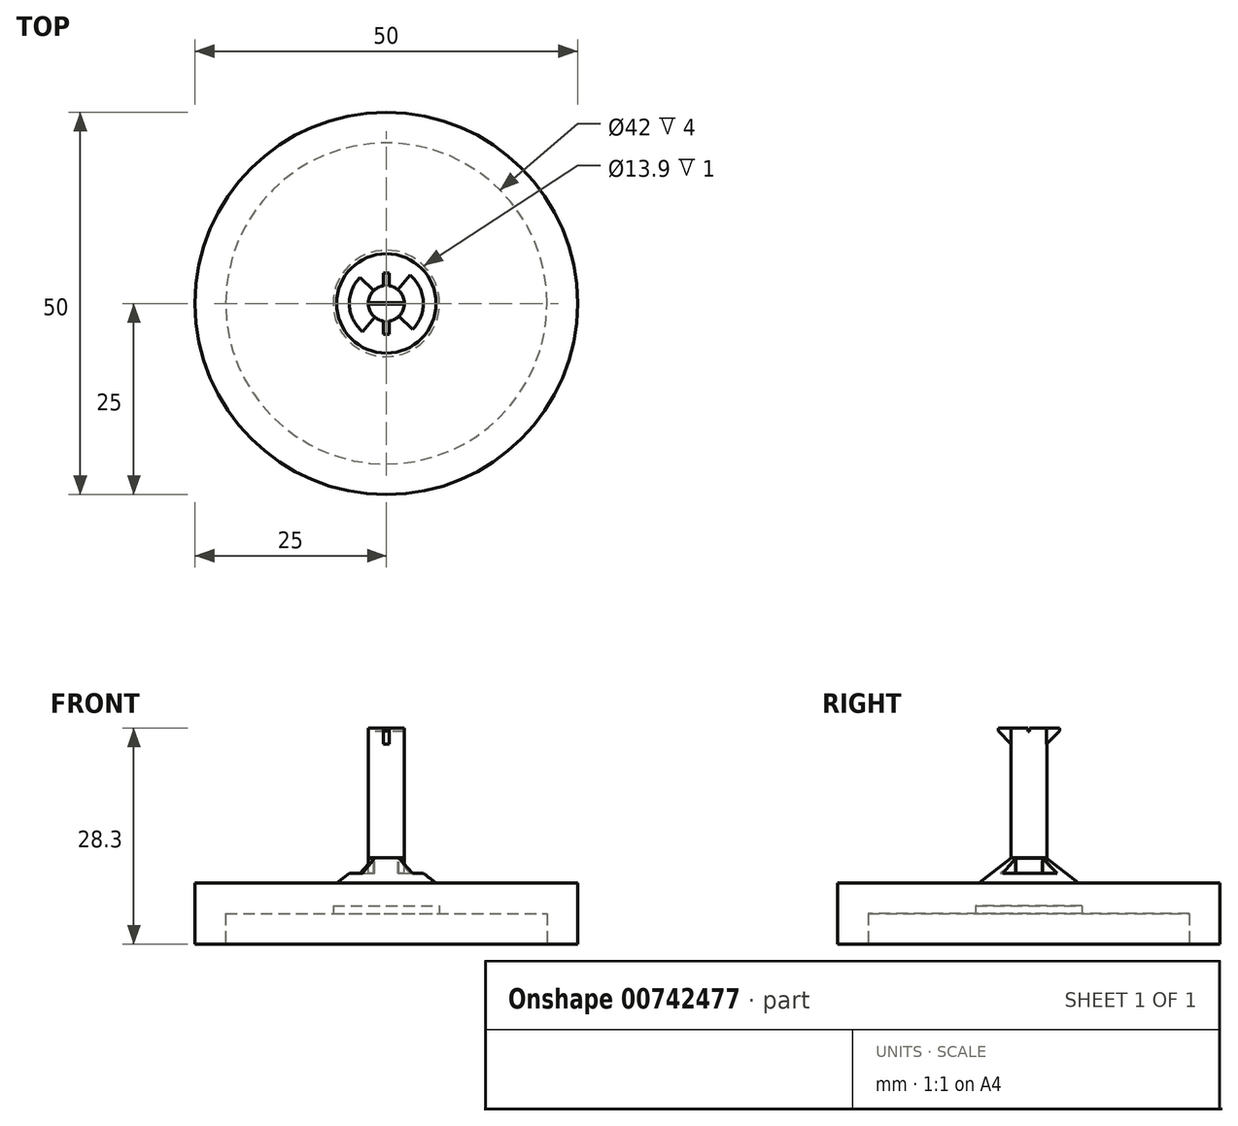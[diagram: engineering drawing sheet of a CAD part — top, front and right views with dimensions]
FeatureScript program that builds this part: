
annotation { "Feature Type Name" : "Feature", "Feature Type Description" : "" }
export const myFeature = defineFeature(function(context is Context, id is Id, definition is map)
    precondition{}
    {
        {
            var Q0;
            Q0=qCreatedBy(makeId("Top.planeOp"),FACE);
            var sketch = newSketch(context, id + "F0", { "sketchPlane" : qUnion([Q0])});
            skCircle(sketch, "E0", {"center": v(0, 0) * mm, "radius": 25 * mm});
            skSolve(sketch);
        }
        {
            var Q0;
            Q0=qSketchRegion(id+"F0",true);
            extrude(context, id + "F1", {"entities" : qUnion([Q0]), "depth" : 8 * mm, "offsetDistance" : 25 * mm});
        }
        {
            var Q0;
            Q0=makeQuery(id+"F1.opExtrude","CAP_FACE",FACE,{"disambiguationData":[OSD([sQuery(id+"F0.wireOp",EDGE,"E0")])],"isStart":true});
            var sketch = newSketch(context, id + "F2", { "sketchPlane" : qUnion([Q0])});
            skCircle(sketch, "E1", {"center": v(0, 0) * mm, "radius": 21 * mm});
            skSolve(sketch);
        }
        {
            var Q0;
            Q0=makeQuery(id+"F2.imprint","IMPRINT",FACE,{"disambiguationData":[TD([[makeQuery(id+"F2.imprint","IMPRINT",EDGE,{"derivedFrom":sQuery(id+"F2.wireOp",EDGE,"E1")}),1.0]])]});
            extrude(context, id + "F3", {"entities" : qUnion([Q0]), "operationType" : NewBodyOperationType.REMOVE, "oppositeDirection" : true, "depth" : 4 * mm, "offsetDistance" : 25 * mm});
        }
        {
            var Q0;
            Q0=makeQuery(id+"F3.boolean.opBoolean","COPY",FACE,{"derivedFrom":makeQuery(id+"F3.opExtrude","CAP_FACE",FACE,{"disambiguationData":[OSD([sQuery(id+"F2.wireOp",EDGE,"E1")])],"isStart":false})});
            var sketch = newSketch(context, id + "F4", { "sketchPlane" : qUnion([Q0])});
            skCircle(sketch, "E2", {"center": v(0, 0) * mm, "radius": 6.95 * mm});
            skSolve(sketch);
        }
        {
            var Q0;
            Q0=qSketchRegion(id+"F4",true);
            extrude(context, id + "F5", {"entities" : qUnion([Q0]), "operationType" : NewBodyOperationType.REMOVE, "oppositeDirection" : true, "depth" : 1 * mm, "offsetDistance" : 25 * mm});
        }
        {
            var Q0;
            Q0=makeQuery(id+"F1.opExtrude","CAP_FACE",FACE,{"disambiguationData":[OSD([sQuery(id+"F0.wireOp",EDGE,"E0")])],"isStart":false});
            var sketch = newSketch(context, id + "F6", { "sketchPlane" : qUnion([Q0])});
            skCircle(sketch, "E3", {"center": v(0, 0) * mm, "radius": 6.5 * mm});
            skSolve(sketch);
        }
        {
            var Q0;
            Q0=makeQuery(id+"F6.imprint","IMPRINT",FACE,{"disambiguationData":[TD([[makeQuery(id+"F6.imprint","IMPRINT",EDGE,{"derivedFrom":sQuery(id+"F6.wireOp",EDGE,"E3")}),1.0]])]});
            var Q1;
            Q1=qSketchRegion(id+"F12",true);
            extrude(context, id + "F7", {"entities" : qUnion([Q0, Q1]), "operationType" : NewBodyOperationType.ADD, "depth" : 3.3 * mm, "offsetDistance" : 25 * mm, "hasDraft" : true, "draftAngle" : 52 * degree, "draftPullDirection" : true});
        }
        {
            var Q0;
            Q0=makeQuery(id+"F7.opExtrude","CAP_FACE",FACE,{"disambiguationData":[OSD([sQuery(id+"F6.wireOp",EDGE,"E3")])],"isStart":false});
            var sketch = newSketch(context, id + "F8", { "sketchPlane" : qUnion([Q0])});
            skCircle(sketch, "E4", {"center": v(0, 0) * mm, "radius": 2.35 * mm});
            skSolve(sketch);
        }
        {
            var Q0;
            Q0=qSketchRegion(id+"F8",true);
            extrude(context, id + "F9", {"entities" : qUnion([Q0]), "operationType" : NewBodyOperationType.ADD, "depth" : 17 * mm, "offsetDistance" : 25 * mm});
        }
        {
            var Q0;
            Q0=makeQuery(id+"F9.opExtrude","CAP_FACE",FACE,{"disambiguationData":[OSD([sQuery(id+"F8.wireOp",EDGE,"E4")])],"isStart":false});
            var sketch = newSketch(context, id + "F10", { "sketchPlane" : qUnion([Q0])});
            skLineSegment(sketch, "E5.bottom", {"start": v(0.35, -4) * mm, "end": v(-0.35, -4) * mm});
            skLineSegment(sketch, "E5.top", {"start": v(0.35, 4) * mm, "end": v(-0.35, 4) * mm});
            skLineSegment(sketch, "E5.left", {"start": v(0.35, -4) * mm, "end": v(0.35, 4) * mm});
            skLineSegment(sketch, "E5.right", {"start": v(-0.35, -4) * mm, "end": v(-0.35, 4) * mm});
            skPoint(sketch, "E5.middle", {"position": v(0, 0) * mm});
            skSolve(sketch);
        }
        {
            var Q0;
            {var subQ0=sQuery(id+"F10.wireOp",EDGE,"E5.top");Q0=makeQuery(id+"F10.imprint","IMPRINT",FACE,{"disambiguationData":[TD([[makeQuery(id+"F10.imprint","IMPRINT",EDGE,{"derivedFrom":subQ0}),1.0]])]});}
            var Q1;
            {var subQ0=sQuery(id+"F10.wireOp",EDGE,"E5.left");var subQ1=makeQuery(id+"F9.opExtrude","CAP_EDGE",EDGE,{"disambiguationData":[OSD([sQuery(id+"F8.wireOp",EDGE,"E4")])],"isStart":false});var subQ2=makeQuery(id+"F10.imprint","INTERSECT",VERTEX,{"disambiguationData":[OD(0.0)],"derivedFrom":[subQ1,subQ0]});Q1=makeQuery(id+"F10.imprint","IMPRINT",FACE,{"disambiguationData":[TD([[makeQuery(id+"F10.imprint","IMPRINT",EDGE,{"disambiguationData":[TD([[subQ2,-1.0]])],"derivedFrom":subQ0}),1.0]])]});}
            var Q2;
            {var subQ0=sQuery(id+"F10.wireOp",EDGE,"E5.bottom");Q2=makeQuery(id+"F10.imprint","IMPRINT",FACE,{"disambiguationData":[TD([[makeQuery(id+"F10.imprint","IMPRINT",EDGE,{"derivedFrom":subQ0}),-1.0]])]});}
            extrude(context, id + "F11", {"entities" : qUnion([Q0, Q1, Q2]), "operationType" : NewBodyOperationType.ADD, "oppositeDirection" : true, "depth" : 2.1 * mm, "offsetDistance" : 25 * mm, "hasDraft" : true, "draftAngle" : 0 * degree, "draftPullDirection" : true});
        }
        {
            var Q0;
            Q0=makeQuery(id+"F5.boolean.opBoolean","COPY",FACE,{"derivedFrom":makeQuery(id+"F5.opExtrude","CAP_FACE",FACE,{"disambiguationData":[OSD([sQuery(id+"F4.wireOp",EDGE,"E2")])],"isStart":false})});
            var sketch = newSketch(context, id + "F12", { "sketchPlane" : qUnion([Q0])});
            skPoint(sketch, "E6", {"position": v(0, 0) * mm});
            skSolve(sketch);
        }
        {
            var Q0;
            Q0=makeQuery(id+"F8.imprint","IMPRINT",FACE,{"disambiguationData":[TD([[makeQuery(id+"F8.imprint","IMPRINT",EDGE,{"derivedFrom":sQuery(id+"F8.wireOp",EDGE,"E4")}),1.0]])]});
            var sketch = newSketch(context, id + "F13", { "sketchPlane" : qUnion([Q0])});
            skLineSegment(sketch, "E7", {"start": v(-5.14, -6.13) * mm, "end": v(5.14, 6.13) * mm});
            skLineSegment(sketch, "E8", {"start": v(-5.66, 5.66) * mm, "end": v(5.66, -5.66) * mm});
            skLineSegment(sketch, "E9", {"start": v(-5.66, 5.66) * mm, "end": v(-5.14, -6.13) * mm});
            skLineSegment(sketch, "E10", {"start": v(5.14, 6.13) * mm, "end": v(5.66, -5.66) * mm});
            skSolve(sketch);
        }
        {
            var Q0;
            {var subQ0=sQuery(id+"F13.wireOp",EDGE,"E10");Q0=makeQuery(id+"F13.imprint","IMPRINT",FACE,{"disambiguationData":[TD([[makeQuery(id+"F13.imprint","IMPRINT",EDGE,{"derivedFrom":subQ0}),-1.0]])]});}
            var Q1;
            {var subQ0=sQuery(id+"F13.wireOp",EDGE,"E9");Q1=makeQuery(id+"F13.imprint","IMPRINT",FACE,{"disambiguationData":[TD([[makeQuery(id+"F13.imprint","IMPRINT",EDGE,{"derivedFrom":subQ0}),1.0]])]});}
            extrude(context, id + "F14", {"entities" : qUnion([Q0, Q1]), "operationType" : NewBodyOperationType.REMOVE, "oppositeDirection" : true, "depth" : 2 * mm, "offsetDistance" : 25 * mm});
        }
        {
            var Q0;
            {var subQ0=sQuery(id+"F10.wireOp",EDGE,"E5.right");var subQ2=sQuery(id+"F10.wireOp",EDGE,"E5.top");Q0=makeQuery(id+"F11.boolean.opBoolean","SPLIT",FACE,{"disambiguationData":[TD([makeQuery(id+"F11.opExtrude","SWEPT_FACE",FACE,{"disambiguationData":[OSD([subQ2])]})])],"derivedFrom":makeQuery(id+"F11.opExtrude","SWEPT_FACE",FACE,{"disambiguationData":[OSD([subQ0])]})});}
            var sketch = newSketch(context, id + "F15", { "sketchPlane" : qUnion([Q0])});
            skLineSegment(sketch, "E11", {"start": v(-2.32, 26.2) * mm, "end": v(-4, 27.9) * mm});
            skLineSegment(sketch, "E12", {"start": v(-4, 27.9) * mm, "end": v(-4, 28.3) * mm});
            skSolve(sketch);
        }
        {
            var Q0;
            {var subQ0=sQuery(id+"F10.wireOp",EDGE,"E5.bottom");var subQ2=sQuery(id+"F10.wireOp",EDGE,"E5.right");Q0=makeQuery(id+"F11.boolean.opBoolean","SPLIT",FACE,{"disambiguationData":[TD([makeQuery(id+"F11.opExtrude","SWEPT_FACE",FACE,{"disambiguationData":[OSD([subQ0])]})])],"derivedFrom":makeQuery(id+"F11.opExtrude","SWEPT_FACE",FACE,{"disambiguationData":[OSD([subQ2])]})});}
            var sketch = newSketch(context, id + "F16", { "sketchPlane" : qUnion([Q0])});
            skLineSegment(sketch, "E13", {"start": v(2.32, 26.2) * mm, "end": v(4, 27.9) * mm});
            skLineSegment(sketch, "E14", {"start": v(4, 27.9) * mm, "end": v(4, 28.3) * mm});
            skSolve(sketch);
        }
        {
            var Q0;
            {var subQ0=sQuery(id+"F16.wireOp",EDGE,"E13");Q0=makeQuery(id+"F16.imprint","IMPRINT",FACE,{"disambiguationData":[TD([[makeQuery(id+"F16.imprint","IMPRINT",EDGE,{"derivedFrom":subQ0}),-1.0]])]});}
            extrude(context, id + "F17", {"entities" : qUnion([Q0]), "operationType" : NewBodyOperationType.REMOVE, "oppositeDirection" : true, "depth" : 25 * mm, "offsetDistance" : 25 * mm});
        }
        {
            var Q0;
            {var subQ0=sQuery(id+"F15.wireOp",EDGE,"E11");Q0=makeQuery(id+"F15.imprint","IMPRINT",FACE,{"disambiguationData":[TD([[makeQuery(id+"F15.imprint","IMPRINT",EDGE,{"derivedFrom":subQ0}),1.0]])]});}
            extrude(context, id + "F18", {"entities" : qUnion([Q0]), "operationType" : NewBodyOperationType.REMOVE, "oppositeDirection" : true, "depth" : 25 * mm, "offsetDistance" : 25 * mm});
        }
        {
            var Q0;
            Q0=makeQuery(id+"F11.boolean.opBoolean","MERGE",FACE,{"derivedFrom":[makeQuery(id+"F9.opExtrude","CAP_FACE",FACE,{"disambiguationData":[OSD([sQuery(id+"F8.wireOp",EDGE,"E4")])],"isStart":false}),makeQuery(id+"F11.opExtrude","CAP_FACE",FACE,{"disambiguationData":[OSD([sQuery(id+"F10.wireOp",EDGE,"E5.bottom"),sQuery(id+"F10.wireOp",EDGE,"E5.top"),sQuery(id+"F10.wireOp",EDGE,"E5.left"),sQuery(id+"F10.wireOp",EDGE,"E5.right")])],"isStart":true})]});
            var sketch = newSketch(context, id + "F19", { "sketchPlane" : qUnion([Q0])});
            skLineSegment(sketch, "E15.bottom", {"start": v(3, -0.1) * mm, "end": v(-3, -0.1) * mm});
            skLineSegment(sketch, "E15.top", {"start": v(3, 0.1) * mm, "end": v(-3, 0.1) * mm});
            skLineSegment(sketch, "E15.left", {"start": v(3, -0.1) * mm, "end": v(3, 0.1) * mm});
            skLineSegment(sketch, "E15.right", {"start": v(-3, -0.1) * mm, "end": v(-3, 0.1) * mm});
            skPoint(sketch, "E15.middle", {"position": v(0, 0) * mm});
            skSolve(sketch);
        }
        {
            var Q0;
            {var subQ0=sQuery(id+"F19.wireOp",EDGE,"E15.right");Q0=makeQuery(id+"F19.imprint","IMPRINT",FACE,{"disambiguationData":[TD([[makeQuery(id+"F19.imprint","IMPRINT",EDGE,{"derivedFrom":subQ0}),-1.0]])]});}
            var Q1;
            {var subQ0=sQuery(id+"F19.wireOp",EDGE,"E15.bottom");var subQ1=sQuery(id+"F8.wireOp",EDGE,"E4");var subQ4=sQuery(id+"F10.wireOp",EDGE,"E5.left");var subQ7=makeQuery(id+"F9.opExtrude","CAP_EDGE",EDGE,{"disambiguationData":[OSD([subQ1])],"isStart":false});var subQ8=makeQuery(id+"F11.boolean.opBoolean","SPLIT",EDGE,{"disambiguationData":[TD([makeQuery(id+"F11.opExtrude","SWEPT_FACE",FACE,{"disambiguationData":[OSD([subQ4])]})])],"derivedFrom":subQ7});var subQ9=makeQuery(id+"F19.imprint","INTERSECT",VERTEX,{"derivedFrom":[subQ8,subQ0]});Q1=makeQuery(id+"F19.imprint","IMPRINT",FACE,{"disambiguationData":[TD([[makeQuery(id+"F19.imprint","IMPRINT",EDGE,{"disambiguationData":[TD([[subQ9,-1.0]])],"derivedFrom":subQ0}),-1.0]])]});}
            var Q2;
            {var subQ0=sQuery(id+"F19.wireOp",EDGE,"E15.left");Q2=makeQuery(id+"F19.imprint","IMPRINT",FACE,{"disambiguationData":[TD([[makeQuery(id+"F19.imprint","IMPRINT",EDGE,{"derivedFrom":subQ0}),1.0]])]});}
            extrude(context, id + "F20", {"entities" : qUnion([Q0, Q1, Q2]), "operationType" : NewBodyOperationType.REMOVE, "oppositeDirection" : true, "depth" : 0.5 * mm, "offsetDistance" : 25 * mm});
        }
    });
